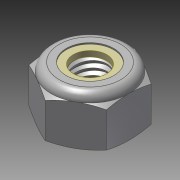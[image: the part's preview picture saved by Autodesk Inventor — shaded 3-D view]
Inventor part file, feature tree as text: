
AUTODESK INVENTOR PART (.ipt)
format: ipt  version: 2014 SP1 (Build 180222100, 222)  size: 348,160 bytes
history: native  units: in
note: dims shown in document units (in); Inventor stores cm internally (conversion verified against a paired STEP export)
features: other x2, imported_body x2, revolve x1
ambient origin geometry x8: Origin, YZ Plane, XZ Plane, XY Plane, X Axis, Y Axis, Z Axis, Center Point
bodies: Body1 (feature_tree), Body2 (feature_tree)
feature tree (5):
  other  "Cut-Revolve4"
  other  "217-3421-010 Rev1.ipt1"
  revolve  "Revolve2"  [1 undecoded]
  imported_body  "Base1"
  imported_body  "Base2"
note: 1 required parameter value undecoded (feature->parameter linkage not recoverable at this tier; creation-order binding heuristic only, values carry confidence <= 0.55)
